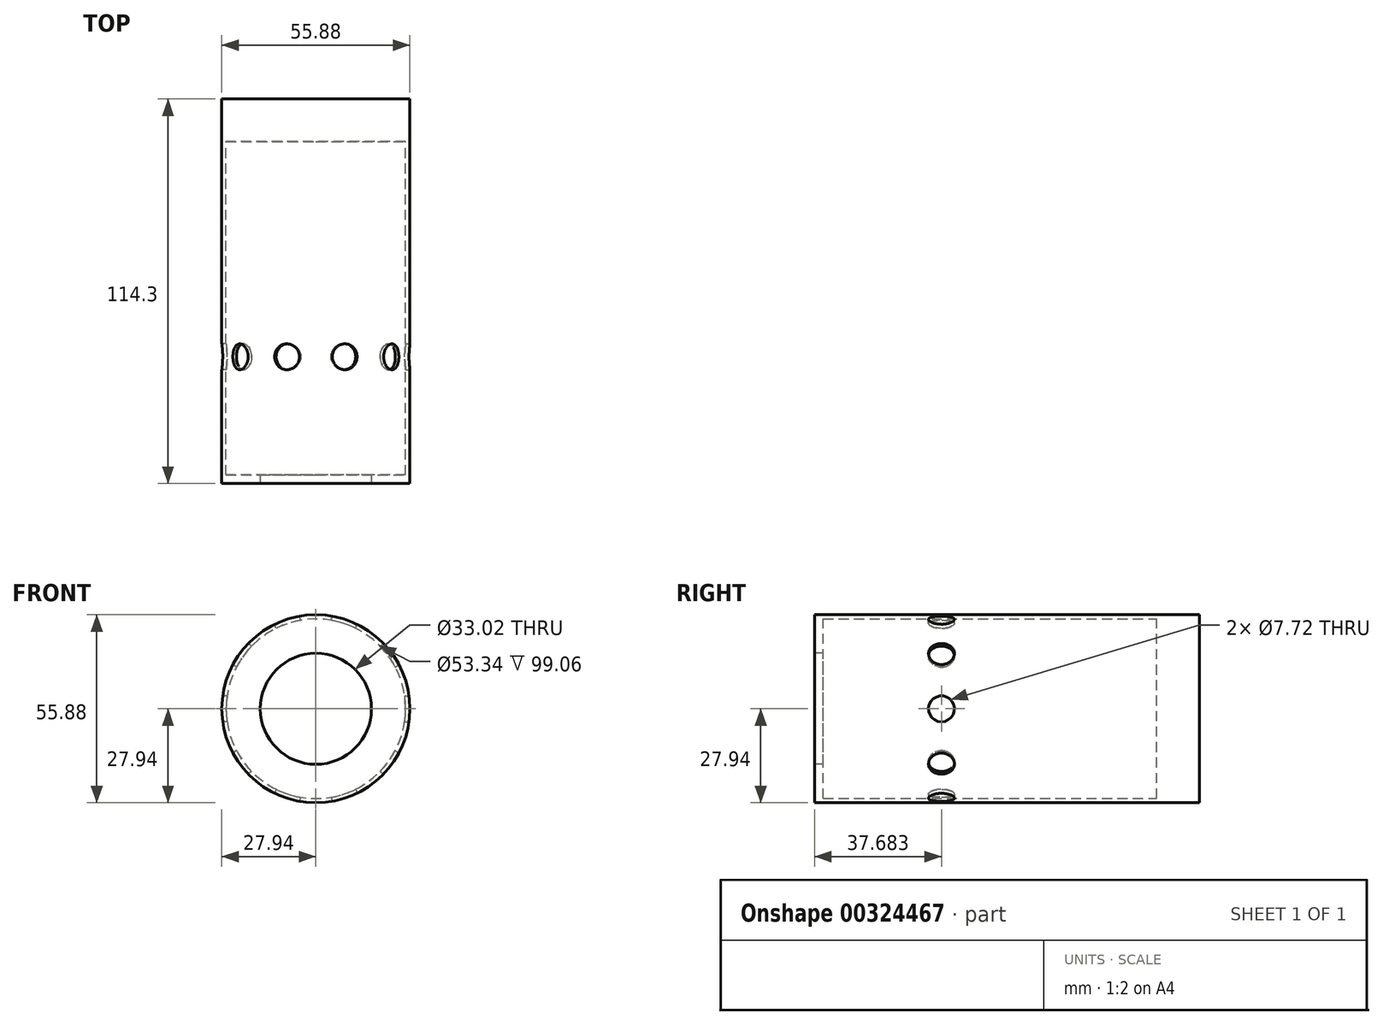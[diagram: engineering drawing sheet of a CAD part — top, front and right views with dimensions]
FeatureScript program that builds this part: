
annotation { "Feature Type Name" : "Feature", "Feature Type Description" : "" }
export const myFeature = defineFeature(function(context is Context, id is Id, definition is map)
    precondition{}
    {
        {
            var Q0;
            Q0=qCreatedBy(makeId("Front.planeOp"),FACE);
            var sketch = newSketch(context, id + "F0", { "sketchPlane" : qUnion([Q0])});
            skCircle(sketch, "E0", {"center": v(0, 0) * mm, "radius": 27.94 * mm});
            skSolve(sketch);
        }
        {
            var Q0;
            Q0=makeQuery(id+"F0.imprint","IMPRINT",FACE,{"disambiguationData":[TD([[makeQuery(id+"F0.imprint","IMPRINT",EDGE,{"derivedFrom":sQuery(id+"F0.wireOp",EDGE,"E0")}),1.0]])]});
            extrude(context, id + "F1", {"entities" : qUnion([Q0]), "depth" : 114.3 * mm});
        }
        {
            var Q0;
            Q0=makeQuery(id+"F1.opExtrude","CAP_FACE",FACE,{"disambiguationData":[OSD([sQuery(id+"F0.wireOp",EDGE,"E0")])],"isStart":false});
            var sketch = newSketch(context, id + "F2", { "sketchPlane" : qUnion([Q0])});
            skCircle(sketch, "E1", {"center": v(0, 0) * mm, "radius": 16.51 * mm});
            skSolve(sketch);
        }
        {
            var Q0;
            Q0 = qSketchRegion(id + "F2", true);
            extrude(context, id + "F3", {"entities" : qUnion([Q0]), "operationType" : NewBodyOperationType.REMOVE, "oppositeDirection" : true, "depth" : 116.84 * mm});
        }
        {
            var Q0;
            Q0=qCreatedBy(makeId("Right.planeOp"),FACE);
            var sketch = newSketch(context, id + "F4", { "sketchPlane" : qUnion([Q0])});
            skCircle(sketch, "E2", {"center": v(-76.62, 0) * mm, "radius": 3.86 * mm});
            skSolve(sketch);
        }
        {
            var Q0;
            Q0 = qSketchRegion(id + "F4", true);
            extrude(context, id + "F5", {"entities" : qUnion([Q0]), "operationType" : NewBodyOperationType.REMOVE, "endBound" : BoundingType.SYMMETRIC, "oppositeDirection" : true, "depth" : 304.8 * mm});
        }
        {
            var Q0;
            Q0=qCreatedBy(makeId("Front.planeOp"),FACE);
            var sketch = newSketch(context, id + "F6", { "sketchPlane" : qUnion([Q0])});
            skCircle(sketch, "E3", {"center": v(0, 0) * mm, "radius": 26.67 * mm});
            skSolve(sketch);
        }
        {
            var Q0;
            Q0 = qSketchRegion(id + "F6", true);
            extrude(context, id + "F7", {"entities" : qUnion([Q0]), "operationType" : NewBodyOperationType.REMOVE, "depth" : 111.76 * mm});
        }
        {
            var Q0;
            Q0=makeQuery(id+"F0.imprint","IMPRINT",FACE,{"disambiguationData":[TD([[makeQuery(id+"F0.imprint","IMPRINT",EDGE,{"derivedFrom":sQuery(id+"F0.wireOp",EDGE,"E0")}),1.0]])]});
            extrude(context, id + "F8", {"entities" : qUnion([Q0]), "operationType" : NewBodyOperationType.ADD, "depth" : 12.7 * mm});
        }
        {
            var Q0;
            Q0=makeQuery(id+"F5.boolean.opBoolean","COPY",FACE,{"disambiguationData":[OD(1.0)],"derivedFrom":makeQuery(id+"F5.opExtrude","SWEPT_FACE",FACE,{"disambiguationData":[OSD([sQuery(id+"F4.wireOp",EDGE,"E2")])]})});
            var Q1;
            Q1=makeQuery(id+"F1.opExtrude","SWEPT_FACE",FACE,{"disambiguationData":[OSD([sQuery(id+"F0.wireOp",EDGE,"E0")])]});
            circularPattern(context, id + "F9", {"patternType" : PatternType.FACE, "operationType" : NewBodyOperationType.ADD, "faces" : qUnion([Q0]), "axis" : qUnion([Q1]), "angle" : 360 * degree, "instanceCount" : 10, "oppositeDirection" : true, "equalSpace" : true});
        }
        {
            var Q0;
            Q0 = qSketchRegion(id + "F6", true);
            extrude(context, id + "F10", {"entities" : qUnion([Q0]), "operationType" : NewBodyOperationType.ADD, "depth" : 7.62 * mm});
        }
    });
